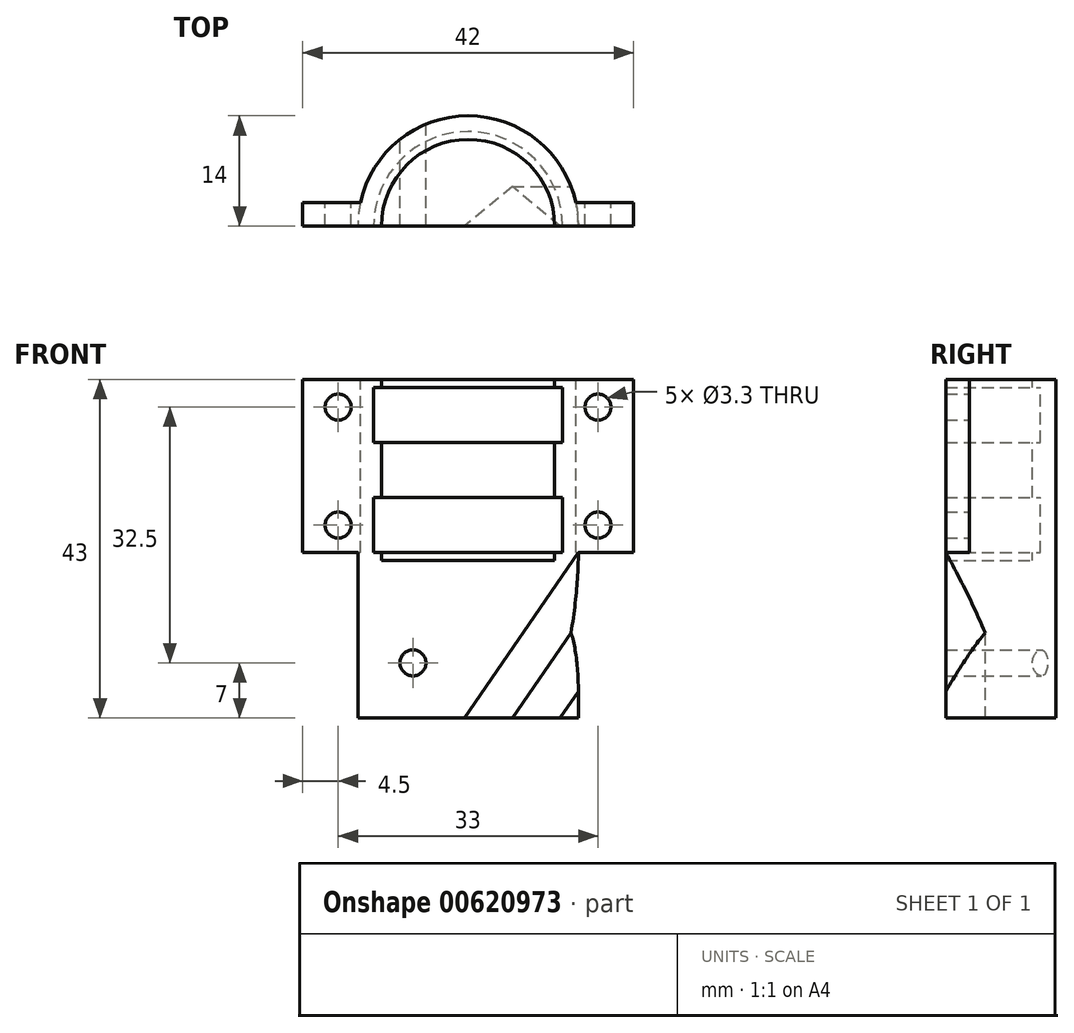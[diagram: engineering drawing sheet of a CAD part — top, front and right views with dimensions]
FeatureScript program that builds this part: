
annotation { "Feature Type Name" : "Feature", "Feature Type Description" : "" }
export const myFeature = defineFeature(function(context is Context, id is Id, definition is map)
    precondition{}
    {
        {
            var Q0;
            Q0=qCreatedBy(makeId("Front.planeOp"),FACE);
            var sketch = newSketch(context, id + "F0", { "sketchPlane" : qUnion([Q0])});
            skLineSegment(sketch, "E0", {"start": v(-11, 21) * mm, "end": v(-12, 21) * mm});
            skLineSegment(sketch, "E1", {"start": v(-12, 21) * mm, "end": v(-12, 14) * mm});
            skLineSegment(sketch, "E2", {"start": v(-12, 14) * mm, "end": v(-11, 14) * mm});
            skLineSegment(sketch, "E3", {"start": v(-11, 14) * mm, "end": v(-11, 7) * mm});
            skLineSegment(sketch, "E4", {"start": v(-11, 7) * mm, "end": v(-12, 7) * mm});
            skLineSegment(sketch, "E5", {"start": v(-12, 7) * mm, "end": v(-12, 0) * mm});
            skLineSegment(sketch, "E6", {"start": v(-12, 0) * mm, "end": v(-11, 0) * mm});
            skLineSegment(sketch, "E7", {"start": v(-11, 0) * mm, "end": v(-11, -1) * mm});
            skLineSegment(sketch, "E8", {"start": v(-11, -1) * mm, "end": v(0, -1) * mm});
            skLineSegment(sketch, "E9", {"start": v(0, -1) * mm, "end": v(0, -21) * mm});
            skLineSegment(sketch, "E10", {"start": v(0, -21) * mm, "end": v(-14, -21) * mm});
            skLineSegment(sketch, "E11", {"start": v(-14, -21) * mm, "end": v(-14, 22) * mm});
            skLineSegment(sketch, "E12", {"start": v(-14, 22) * mm, "end": v(-11, 22) * mm});
            skLineSegment(sketch, "E13", {"start": v(-11, 22) * mm, "end": v(-11, 21) * mm});
            skSolve(sketch);
        }
        {
            var Q0;
            Q0 = qSketchRegion(id + "F0", true);
            var Q1;
            Q1=sQuery(id+"F0.wireOp",EDGE,"E9");
            revolve(context, id + "F1", {"entities" : qUnion([Q0]), "axis" : qUnion([Q1]), "revolveType" : RevolveType.ONE_DIRECTION, "angle" : 180 * degree});
        }
        {
            var Q0;
            Q0=makeQuery(id+"F1.opRevolve","CAP_FACE",FACE,{"disambiguationData":[OSD([sQuery(id+"F0.wireOp",EDGE,"E0"),sQuery(id+"F0.wireOp",EDGE,"E1"),sQuery(id+"F0.wireOp",EDGE,"E2"),sQuery(id+"F0.wireOp",EDGE,"E3"),sQuery(id+"F0.wireOp",EDGE,"E4"),sQuery(id+"F0.wireOp",EDGE,"E5"),sQuery(id+"F0.wireOp",EDGE,"E6"),sQuery(id+"F0.wireOp",EDGE,"E7"),sQuery(id+"F0.wireOp",EDGE,"E8"),sQuery(id+"F0.wireOp",EDGE,"E9"),sQuery(id+"F0.wireOp",EDGE,"E10"),sQuery(id+"F0.wireOp",EDGE,"E11"),sQuery(id+"F0.wireOp",EDGE,"E12"),sQuery(id+"F0.wireOp",EDGE,"E13")])],"isStart":false});
            var sketch = newSketch(context, id + "F2", { "sketchPlane" : qUnion([Q0])});
            skLineSegment(sketch, "E14.bottom", {"start": v(-12, 22) * mm, "end": v(-21, 22) * mm});
            skLineSegment(sketch, "E14.top", {"start": v(-12, 0) * mm, "end": v(-21, 0) * mm});
            skLineSegment(sketch, "E14.left", {"start": v(-12, 22) * mm, "end": v(-12, 0) * mm});
            skLineSegment(sketch, "E14.right", {"start": v(-21, 22) * mm, "end": v(-21, 0) * mm});
            skLineSegment(sketch, "E15", {"start": v(0, 0) * mm, "end": v(0, -21) * mm, "construction": true});
            skPoint(sketch, "E16", {"position": v(-16.5, 18.5) * mm});
            skPoint(sketch, "E16.positionSnap0", {"position": v(-16.5, 22) * mm});
            skPoint(sketch, "E17", {"position": v(-16.5, 3.5) * mm});
            skPoint(sketch, "E18", {"position": v(-7, -14) * mm});
            skPoint(sketch, "E19.MirrorP", {"position": v(16.5, 3.5) * mm});
            skPoint(sketch, "E20.MirrorP", {"position": v(16.5, 18.5) * mm});
            skLineSegment(sketch, "E21.MirrorCS", {"start": v(21, 22) * mm, "end": v(21, 0) * mm});
            skLineSegment(sketch, "E22.MirrorCS", {"start": v(12, 22) * mm, "end": v(12, 0) * mm});
            skLineSegment(sketch, "E23.MirrorCS", {"start": v(12, 0) * mm, "end": v(21, 0) * mm});
            skLineSegment(sketch, "E24.MirrorCS", {"start": v(12, 22) * mm, "end": v(21, 22) * mm});
            skSolve(sketch);
        }
        {
            var Q0;
            Q0 = qSketchRegion(id + "F2", true);
            extrude(context, id + "F3", {"entities" : qUnion([Q0]), "operationType" : NewBodyOperationType.ADD, "oppositeDirection" : true, "depth" : 3 * mm, "offsetDistance" : 25 * mm});
        }
        {
            var Q0;
            Q0=sQuery(id+"F2.wireOp",VERTEX,"E16");
            var Q1;
            Q1=sQuery(id+"F2.wireOp",VERTEX,"E17");
            var Q2;
            Q2=sQuery(id+"F2.wireOp",VERTEX,"E18");
            var Q3;
            Q3=sQuery(id+"F2.wireOp",VERTEX,"E20.MirrorP");
            var Q4;
            Q4=sQuery(id+"F2.wireOp",VERTEX,"E19.MirrorP");
            var Q5;
            Q5=makeQuery(id+"F1.opRevolve","SWEPT_BODY",BODY,{"disambiguationData":[OSD([sQuery(id+"F0.wireOp",EDGE,"E0"),sQuery(id+"F0.wireOp",EDGE,"E1"),sQuery(id+"F0.wireOp",EDGE,"E2"),sQuery(id+"F0.wireOp",EDGE,"E3"),sQuery(id+"F0.wireOp",EDGE,"E4"),sQuery(id+"F0.wireOp",EDGE,"E5"),sQuery(id+"F0.wireOp",EDGE,"E6"),sQuery(id+"F0.wireOp",EDGE,"E7"),sQuery(id+"F0.wireOp",EDGE,"E8"),sQuery(id+"F0.wireOp",EDGE,"E9"),sQuery(id+"F0.wireOp",EDGE,"E10"),sQuery(id+"F0.wireOp",EDGE,"E11"),sQuery(id+"F0.wireOp",EDGE,"E12"),sQuery(id+"F0.wireOp",EDGE,"E13")])]});
            hole(context, id + "F4", {"style" : HoleStyle.SIMPLE, "endStyle" : HoleEndStyle.THROUGH, "standardTappedOrClearance" : lookupTablePath({ "standard" : "ISO", "fit" : "Normal", "size" : "M3", "type" : "Clearance" }), "standardBlindInLast" : lookupTablePath({ "fit" : "Standard", "standard" : "ISO", "size" : "M3", "type" : "Clearance" }), "holeDiameter" : 3.3 * mm, "majorDiameter" : 5 * mm, "isTappedThrough" : true, "tappedDepth" : 7 * mm, "tapClearance" : 6, "locations" : qUnion([Q0, Q1, Q2, Q3, Q4]), "scope" : qUnion([Q5]), "startStyle" : HoleStartStyle.SKETCH});
        }
        {
            var Q0;
            Q0=makeQuery(id+"F3.opExtrude","CAP_VERTEX",VERTEX,{"disambiguationData":[OSD([sQuery(id+"F2.wireOp",EDGE,"E21.MirrorCS"),sQuery(id+"F2.wireOp",EDGE,"E23.MirrorCS")])],"isStart":true});
            var Q1;
            Q1=makeQuery(id+"F3.opExtrude","CAP_VERTEX",VERTEX,{"disambiguationData":[OSD([sQuery(id+"F2.wireOp",EDGE,"E21.MirrorCS"),sQuery(id+"F2.wireOp",EDGE,"E23.MirrorCS")])],"isStart":false});
            var Q2;
            Q2=makeQuery(id+"F1.opRevolve","CAP_VERTEX",VERTEX,{"disambiguationData":[OSD([sQuery(id+"F0.wireOp",EDGE,"E12"),sQuery(id+"F0.wireOp",EDGE,"E13")])],"isStart":true});
            cPlane(context, id + "F5", {"entities" : qUnion([Q0, Q1, Q2]), "cplaneType" : CPlaneType.THREE_POINT, "offset" : 25 * mm, "width" : 150 * mm, "height" : 150 * mm});
        }
        {
            var Q0;
            Q0=qCreatedBy(id+"F5.planeOp",FACE);
            cPlane(context, id + "F6", {"entities" : qUnion([Q0]), "cplaneType" : CPlaneType.OFFSET, "offset" : 4 * mm, "width" : 150 * mm, "height" : 150 * mm});
        }
        {
            var Q0;
            Q0=qCreatedBy(id+"F6.planeOp",FACE);
            var sketch = newSketch(context, id + "F7", { "sketchPlane" : qUnion([Q0])});
            skLineSegment(sketch, "E25", {"start": v(21.54, 0) * mm, "end": v(16.54, -5) * mm});
            skLineSegment(sketch, "E26", {"start": v(16.54, -5) * mm, "end": v(11.54, 0) * mm});
            skLineSegment(sketch, "E27", {"start": v(11.54, 0) * mm, "end": v(21.54, 0) * mm});
            skSolve(sketch);
        }
        {
            var Q0;
            Q0 = qSketchRegion(id + "F7", true);
            extrude(context, id + "F8", {"entities" : qUnion([Q0]), "operationType" : NewBodyOperationType.REMOVE, "depth" : 30 * mm, "offsetDistance" : 25 * mm});
        }
    });
